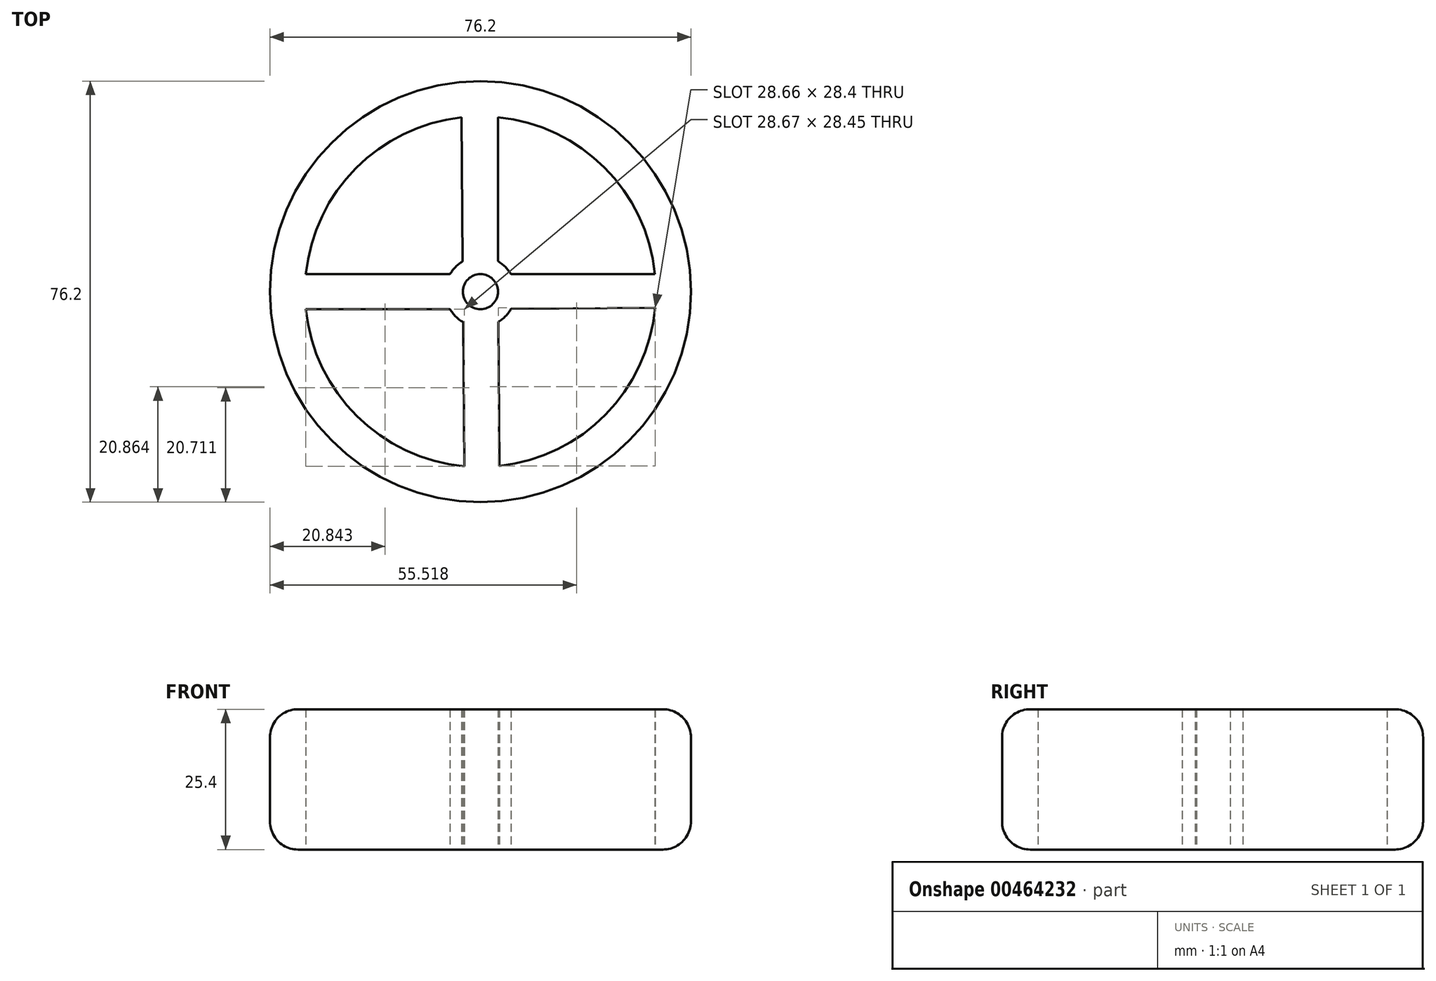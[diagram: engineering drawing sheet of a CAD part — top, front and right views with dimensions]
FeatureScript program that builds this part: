
annotation { "Feature Type Name" : "Feature", "Feature Type Description" : "" }
export const myFeature = defineFeature(function(context is Context, id is Id, definition is map)
    precondition{}
    {
        {
            var Q0;
            Q0=qCreatedBy(makeId("Top.planeOp"),FACE);
            var sketch = newSketch(context, id + "F0", { "sketchPlane" : qUnion([Q0])});
            skCircle(sketch, "E0", {"center": v(0, 0) * mm, "radius": 38.1 * mm});
            skArc(sketch, "E1", {"start": v(-3.43, 31.56) * mm, "mid": v(-22.54, 22.36) * mm, "end": v(-31.6, 3.18) * mm});
            skArc(sketch, "E2", {"start": v(-3.22, 5.47) * mm, "mid": v(-4.5, 4.47) * mm, "end": v(-5.5, 3.18) * mm});
            skCircle(sketch, "E3", {"center": v(0, 0) * mm, "radius": 3.18 * mm});
            skLineSegment(sketch, "E4", {"start": v(-0.28, -3.16) * mm, "end": v(0.33, -3.16) * mm});
            skLineSegment(sketch, "E5", {"start": v(3.22, -5.47) * mm, "end": v(3.43, -31.56) * mm});
            skLineSegment(sketch, "E6", {"start": v(-3.18, 0) * mm, "end": v(-3.17, -0.05) * mm});
            skLineSegment(sketch, "E7", {"start": v(-5.5, -3.16) * mm, "end": v(-31.6, -3.16) * mm});
            skPoint(sketch, "E8.orphan", {"position": v(3.18, 37.97) * mm});
            skLineSegment(sketch, "E9.trimOffspring", {"start": v(-3.48, 37.94) * mm, "end": v(-3.48, 37.97) * mm});
            skLineSegment(sketch, "E10.trimOffspring", {"start": v(-3.22, 5.47) * mm, "end": v(-3.43, 31.56) * mm});
            skLineSegment(sketch, "E11.trimOffspring", {"start": v(-5.5, 3.18) * mm, "end": v(-31.6, 3.18) * mm});
            skArc(sketch, "E12.trimOffspring", {"start": v(-5.5, -3.16) * mm, "mid": v(-4.48, -4.5) * mm, "end": v(-3.13, -5.52) * mm});
            skLineSegment(sketch, "E13.trimOffspring", {"start": v(-3.13, -5.52) * mm, "end": v(-2.92, -31.62) * mm});
            skArc(sketch, "E14.trimOffspring", {"start": v(3.22, -5.47) * mm, "mid": v(4.53, -4.45) * mm, "end": v(5.53, -3.12) * mm});
            skLineSegment(sketch, "E15.trimOffspring", {"start": v(5.53, -3.12) * mm, "end": v(31.62, -2.9) * mm});
            skLineSegment(sketch, "E16.trimOffspring", {"start": v(5.5, 3.18) * mm, "end": v(31.6, 3.18) * mm});
            skLineSegment(sketch, "E17.trimOffspring", {"start": v(3.18, 5.5) * mm, "end": v(3.18, 31.6) * mm});
            skPoint(sketch, "E18.start.orphan", {"position": v(0, 3.18) * mm});
            skArc(sketch, "E19.trimOffspring", {"start": v(5.5, 3.18) * mm, "mid": v(4.5, 4.5) * mm, "end": v(3.18, 5.5) * mm});
            skArc(sketch, "E20.trimOffspring", {"start": v(3.43, -31.56) * mm, "mid": v(22.63, -22.27) * mm, "end": v(31.62, -2.9) * mm});
            skArc(sketch, "E21.trimOffspring", {"start": v(31.6, 3.17) * mm, "mid": v(22.45, 22.45) * mm, "end": v(3.18, 31.6) * mm});
            skArc(sketch, "E22.trimOffspring", {"start": v(-31.6, -3.16) * mm, "mid": v(-22.36, -22.54) * mm, "end": v(-2.92, -31.62) * mm});
            skSolve(sketch);
        }
        {
            var Q0;
            Q0 = qSketchRegion(id + "F0", true);
            extrude(context, id + "F1", {"entities" : qUnion([Q0]), "depth" : 25.4 * mm, "symmetric" : true});
        }
        {
            var Q0;
            Q0=makeQuery(id+"F1.opExtrude","CAP_EDGE",EDGE,{"disambiguationData":[OSD([sQuery(id+"F0.wireOp",EDGE,"E0")])],"isStart":false});
            var Q1;
            Q1=makeQuery(id+"F1.opExtrude","CAP_EDGE",EDGE,{"disambiguationData":[OSD([sQuery(id+"F0.wireOp",EDGE,"E0")])],"isStart":true});
            fillet(context, id + "F2", {"entities" : qUnion([Q0, Q1]), "radius" : 5.08 * mm, "tangentPropagation" : true, "allowEdgeOverflow" : false});
        }
    });
